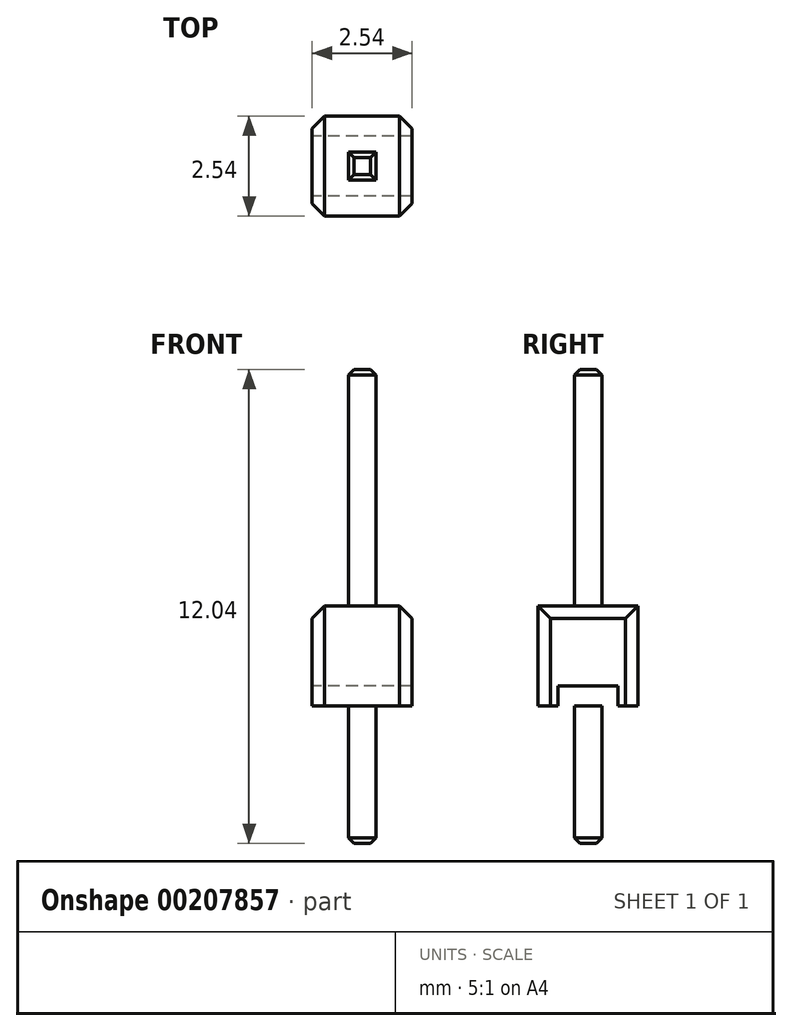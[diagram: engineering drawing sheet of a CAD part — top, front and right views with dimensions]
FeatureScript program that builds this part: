
annotation { "Feature Type Name" : "Feature", "Feature Type Description" : "" }
export const myFeature = defineFeature(function(context is Context, id is Id, definition is map)
    precondition{}
    {
        {
            assignVariable(context, id + "F0", {"name" : "Pitch", "anyValue" : 2.54 * mm});
        }
        {
            assignVariable(context, id + "F1", {"name" : "PinDiameter", "anyValue" : .7 * mm});
        }
        {
            assignVariable(context, id + "F2", {"name" : "PinTop", "anyValue" : 6 * mm});
        }
        {
            assignVariable(context, id + "F3", {"name" : "PinBelow", "anyValue" : 3.5 * mm});
        }
        {
            var Q0;
            Q0=qCreatedBy(makeId("Top.planeOp"),FACE);
            var sketch = newSketch(context, id + "F4", { "sketchPlane" : qUnion([Q0])});
            skLineSegment(sketch, "E0.bottom", {"start": v(-1.27, 1.27) * mm, "end": v(1.27, 1.27) * mm});
            skLineSegment(sketch, "E0.top", {"start": v(-1.27, -1.27) * mm, "end": v(1.27, -1.27) * mm});
            skLineSegment(sketch, "E0.left", {"start": v(-1.27, 1.27) * mm, "end": v(-1.27, -1.27) * mm});
            skLineSegment(sketch, "E0.right", {"start": v(1.27, 1.27) * mm, "end": v(1.27, -1.27) * mm});
            skPoint(sketch, "E0.middle", {"position": v(0, 0) * mm});
            skLineSegment(sketch, "E1.bottom", {"start": v(-0.35, 0.35) * mm, "end": v(0.35, 0.35) * mm});
            skLineSegment(sketch, "E1.top", {"start": v(-0.35, -0.35) * mm, "end": v(0.35, -0.35) * mm});
            skLineSegment(sketch, "E1.left", {"start": v(-0.35, 0.35) * mm, "end": v(-0.35, -0.35) * mm});
            skLineSegment(sketch, "E1.right", {"start": v(0.35, 0.35) * mm, "end": v(0.35, -0.35) * mm});
            skSolve(sketch);
        }
        {
            var Q0;
            Q0=makeQuery(id+"F4.imprint","IMPRINT",FACE,{"disambiguationData":[TD([[makeQuery(id+"F4.imprint","IMPRINT",EDGE,{"derivedFrom":sQuery(id+"F4.wireOp",EDGE,"E0.bottom")}),-1.0]])]});
            var Q1;
            Q1=makeQuery(id+"F4.imprint","IMPRINT",FACE,{"disambiguationData":[TD([[makeQuery(id+"F4.imprint","IMPRINT",EDGE,{"derivedFrom":sQuery(id+"F4.wireOp",EDGE,"E1.bottom")}),-1.0]])]});
            extrude(context, id + "F5", {"entities" : qUnion([Q0, Q1]), "depth" : getVariable(context, 'Pitch')});
        }
        {
            var Q0;
            Q0=makeQuery(id+"F4.imprint","IMPRINT",FACE,{"disambiguationData":[TD([[makeQuery(id+"F4.imprint","IMPRINT",EDGE,{"derivedFrom":sQuery(id+"F4.wireOp",EDGE,"E1.bottom")}),-1.0]])]});
            extrude(context, id + "F6", {"entities" : qUnion([Q0]), "depth" : getVariable(context, 'Pitch') + getVariable(context, 'PinTop')});
        }
        {
            var Q0;
            Q0=makeQuery(id+"F4.imprint","IMPRINT",FACE,{"disambiguationData":[TD([[makeQuery(id+"F4.imprint","IMPRINT",EDGE,{"derivedFrom":sQuery(id+"F4.wireOp",EDGE,"E1.bottom")}),-1.0]])]});
            extrude(context, id + "F7", {"entities" : qUnion([Q0]), "operationType" : NewBodyOperationType.ADD, "oppositeDirection" : true, "depth" : getVariable(context, 'PinBelow')});
        }
        {
            var Q0;
            Q0=makeQuery(id+"F5.opExtrude","SWEPT_FACE",FACE,{"disambiguationData":[OSD([sQuery(id+"F4.wireOp",EDGE,"E0.left")])]});
            var sketch = newSketch(context, id + "F8", { "sketchPlane" : qUnion([Q0])});
            skLineSegment(sketch, "E2", {"start": v(-0.76, 0.5) * mm, "end": v(0.76, 0.5) * mm});
            skLineSegment(sketch, "E3", {"start": v(0.76, 0.5) * mm, "end": v(0.76, 0) * mm});
            skLineSegment(sketch, "E4", {"start": v(0.76, 0) * mm, "end": v(-0.76, 0) * mm});
            skLineSegment(sketch, "E5", {"start": v(-0.76, 0) * mm, "end": v(-0.76, 0.5) * mm});
            skSolve(sketch);
        }
        {
            var Q0;
            Q0=makeQuery(id+"F8.imprint","IMPRINT",FACE,{"disambiguationData":[TD([[makeQuery(id+"F8.imprint","IMPRINT",EDGE,{"derivedFrom":sQuery(id+"F8.wireOp",EDGE,"E2")}),-1.0]])]});
            extrude(context, id + "F9", {"entities" : qUnion([Q0]), "operationType" : NewBodyOperationType.REMOVE, "oppositeDirection" : true, "depth" : 25 * mm});
        }
        {
            var Q0;
            Q0=makeQuery(id+"F5.opExtrude","SWEPT_EDGE",EDGE,{"disambiguationData":[OSD([sQuery(id+"F4.wireOp",EDGE,"E0.top"),sQuery(id+"F4.wireOp",EDGE,"E0.left")])]});
            var Q1;
            Q1=makeQuery(id+"F5.opExtrude","SWEPT_EDGE",EDGE,{"disambiguationData":[OSD([sQuery(id+"F4.wireOp",EDGE,"E0.top"),sQuery(id+"F4.wireOp",EDGE,"E0.right")])]});
            var Q2;
            Q2=makeQuery(id+"F5.opExtrude","SWEPT_EDGE",EDGE,{"disambiguationData":[OSD([sQuery(id+"F4.wireOp",EDGE,"E0.bottom"),sQuery(id+"F4.wireOp",EDGE,"E0.left")])]});
            var Q3;
            Q3=makeQuery(id+"F5.opExtrude","SWEPT_EDGE",EDGE,{"disambiguationData":[OSD([sQuery(id+"F4.wireOp",EDGE,"E0.bottom"),sQuery(id+"F4.wireOp",EDGE,"E0.right")])]});
            var Q4;
            Q4=makeQuery(id+"F5.opExtrude","CAP_EDGE",EDGE,{"disambiguationData":[OSD([sQuery(id+"F4.wireOp",EDGE,"E0.right")])],"isStart":false});
            var Q5;
            Q5=makeQuery(id+"F5.opExtrude","CAP_EDGE",EDGE,{"disambiguationData":[OSD([sQuery(id+"F4.wireOp",EDGE,"E0.left")])],"isStart":false});
            chamfer(context, id + "F10", {"entities" : qUnion([Q0, Q1, Q2, Q3, Q4, Q5]), "width" : getVariable(context, 'Pitch') / 8, "tangentPropagation" : true});
        }
        {
            var Q0;
            Q0=makeQuery(id+"F6.opExtrude","CAP_EDGE",EDGE,{"disambiguationData":[OSD([sQuery(id+"F4.wireOp",EDGE,"E1.left")])],"isStart":false});
            var Q1;
            Q1=makeQuery(id+"F6.opExtrude","CAP_EDGE",EDGE,{"disambiguationData":[OSD([sQuery(id+"F4.wireOp",EDGE,"E1.bottom")])],"isStart":false});
            var Q2;
            Q2=makeQuery(id+"F6.opExtrude","CAP_EDGE",EDGE,{"disambiguationData":[OSD([sQuery(id+"F4.wireOp",EDGE,"E1.top")])],"isStart":false});
            var Q3;
            Q3=makeQuery(id+"F6.opExtrude","CAP_EDGE",EDGE,{"disambiguationData":[OSD([sQuery(id+"F4.wireOp",EDGE,"E1.right")])],"isStart":false});
            var Q4;
            Q4=makeQuery(id+"F7.opExtrude","CAP_FACE",FACE,{"disambiguationData":[OSD([sQuery(id+"F4.wireOp",EDGE,"E1.bottom"),sQuery(id+"F4.wireOp",EDGE,"E1.top"),sQuery(id+"F4.wireOp",EDGE,"E1.left"),sQuery(id+"F4.wireOp",EDGE,"E1.right")])],"isStart":false});
            chamfer(context, id + "F11", {"entities" : qUnion([Q0, Q1, Q2, Q3, Q4]), "width" : getVariable(context, 'PinDiameter') / 5, "tangentPropagation" : true});
        }
    });
